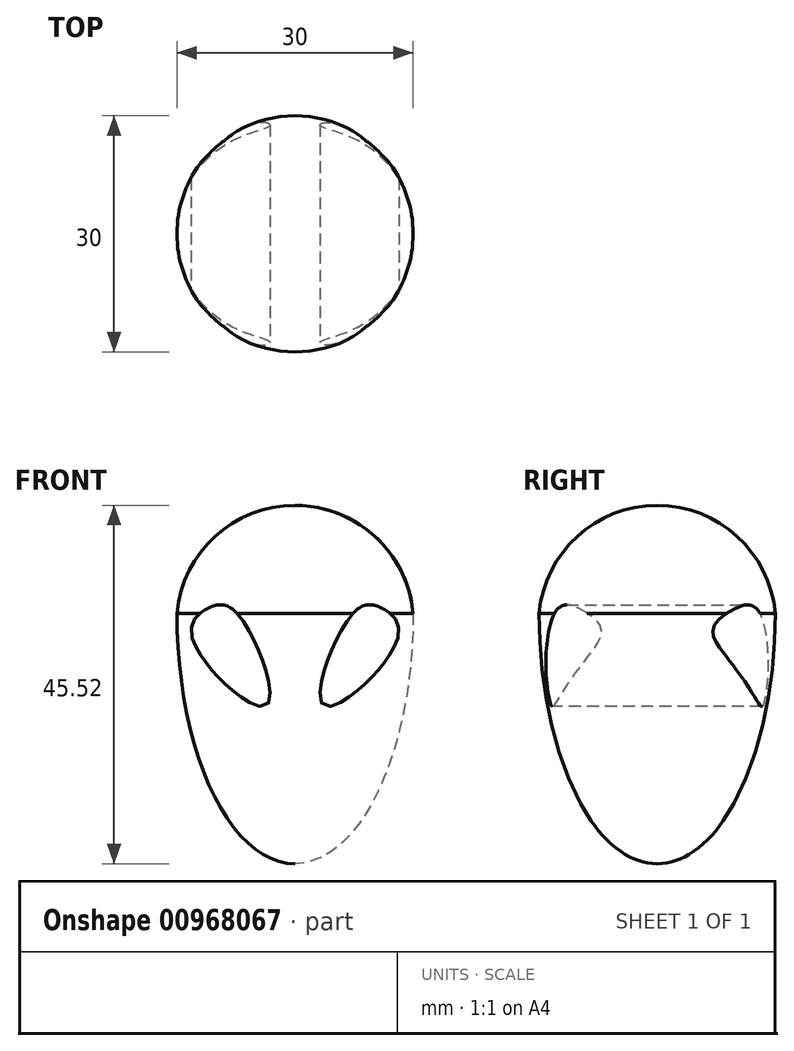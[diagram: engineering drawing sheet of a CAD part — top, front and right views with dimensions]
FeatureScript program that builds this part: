
annotation { "Feature Type Name" : "Feature", "Feature Type Description" : "" }
export const myFeature = defineFeature(function(context is Context, id is Id, definition is map)
    precondition{}
    {
        {
            var Q0;
            Q0=qCreatedBy(makeId("Front.planeOp"),FACE);
            var sketch = newSketch(context, id + "F0", { "sketchPlane" : qUnion([Q0])});
            skEllipticalArc(sketch, "E0", {});
            skArc(sketch, "E1", {"start": v(15, 0) * mm, "mid": v(0, 13.7) * mm, "end": v(-15, 0) * mm});
            skLineSegment(sketch, "E2", {"start": v(-15, 0) * mm, "end": v(15, 0) * mm});
            skLineSegment(sketch, "E3", {"start": v(0, 13.7) * mm, "end": v(0, -31.82) * mm});
            const initialGuessF0  = {"E0": [0, 0, 0, -1, 0.03181702830271166, 0.015, 4.71238898038469, 1.5707963267948966]};
            skSetInitialGuess(sketch, initialGuessF0);
            skSolve(sketch);
        }
        {
            var Q0;
            {var subQ1=sQuery(id+"F0.wireOp",EDGE,"E1");var subQ3=sQuery(id+"F0.wireOp",EDGE,"E3");var subQ4=makeQuery(id+"F0.imprint","INTERSECT",VERTEX,{"derivedFrom":[subQ1,subQ3]});Q0=makeQuery(id+"F0.imprint","IMPRINT",FACE,{"disambiguationData":[TD([[makeQuery(id+"F0.imprint","IMPRINT",EDGE,{"disambiguationData":[TD([[subQ4,-1.0]])],"derivedFrom":subQ3}),-1.0]])]});}
            var Q1;
            {var subQ0=sQuery(id+"F0.wireOp",EDGE,"E3");var subQ1=sQuery(id+"F0.wireOp",EDGE,"E0");var subQ2=makeQuery(id+"F0.imprint","INTERSECT",VERTEX,{"derivedFrom":[subQ1,subQ0]});Q1=makeQuery(id+"F0.imprint","IMPRINT",FACE,{"disambiguationData":[TD([[makeQuery(id+"F0.imprint","IMPRINT",EDGE,{"disambiguationData":[TD([[subQ2,1.0]])],"derivedFrom":subQ0}),-1.0]])]});}
            var Q2;
            Q2=sQuery(id+"F0.wireOp",EDGE,"E3");
            revolve(context, id + "F1", {"surfaceOperationType" : NewSurfaceOperationType.NEW, "entities" : qUnion([Q0, Q1]), "axis" : qUnion([Q2]), "revolveType" : RevolveType.FULL});
        }
        {
            var Q0;
            Q0=qCreatedBy(makeId("Front.planeOp"),FACE);
            var sketch = newSketch(context, id + "F2", { "sketchPlane" : qUnion([Q0])});
            skFitSpline(sketch, "E4", {"points": [v(-10.64, 0.82) * mm, v(-13.1, -3) * mm, v(-3.68, -11.74) * mm, v(-7.07, -0.37) * mm, v(-10.64, 0.82) * mm]});
            skFitSpline(sketch, "E5.MirrorC", {"points": [v(10.64, 0.82) * mm, v(13.1, -3) * mm, v(3.68, -11.74) * mm, v(7.07, -0.37) * mm, v(10.64, 0.82) * mm]});
            skSolve(sketch);
        }
        {
            var Q0;
            Q0=makeQuery(id+"F2.imprint","IMPRINT",FACE,{"disambiguationData":[TD([[makeQuery(id+"F2.imprint","IMPRINT",EDGE,{"derivedFrom":sQuery(id+"F2.wireOp",EDGE,"E4")}),1.0]])]});
            var Q1;
            Q1=makeQuery(id+"F2.imprint","IMPRINT",FACE,{"disambiguationData":[TD([[makeQuery(id+"F2.imprint","IMPRINT",EDGE,{"derivedFrom":sQuery(id+"F2.wireOp",EDGE,"E5.MirrorC")}),-1.0]])]});
            extrude(context, id + "F3", {"entities" : qUnion([Q0, Q1]), "operationType" : NewBodyOperationType.REMOVE, "endBound" : BoundingType.SYMMETRIC, "depth" : 40 * mm, "offsetDistance" : 25 * mm});
        }
    });
